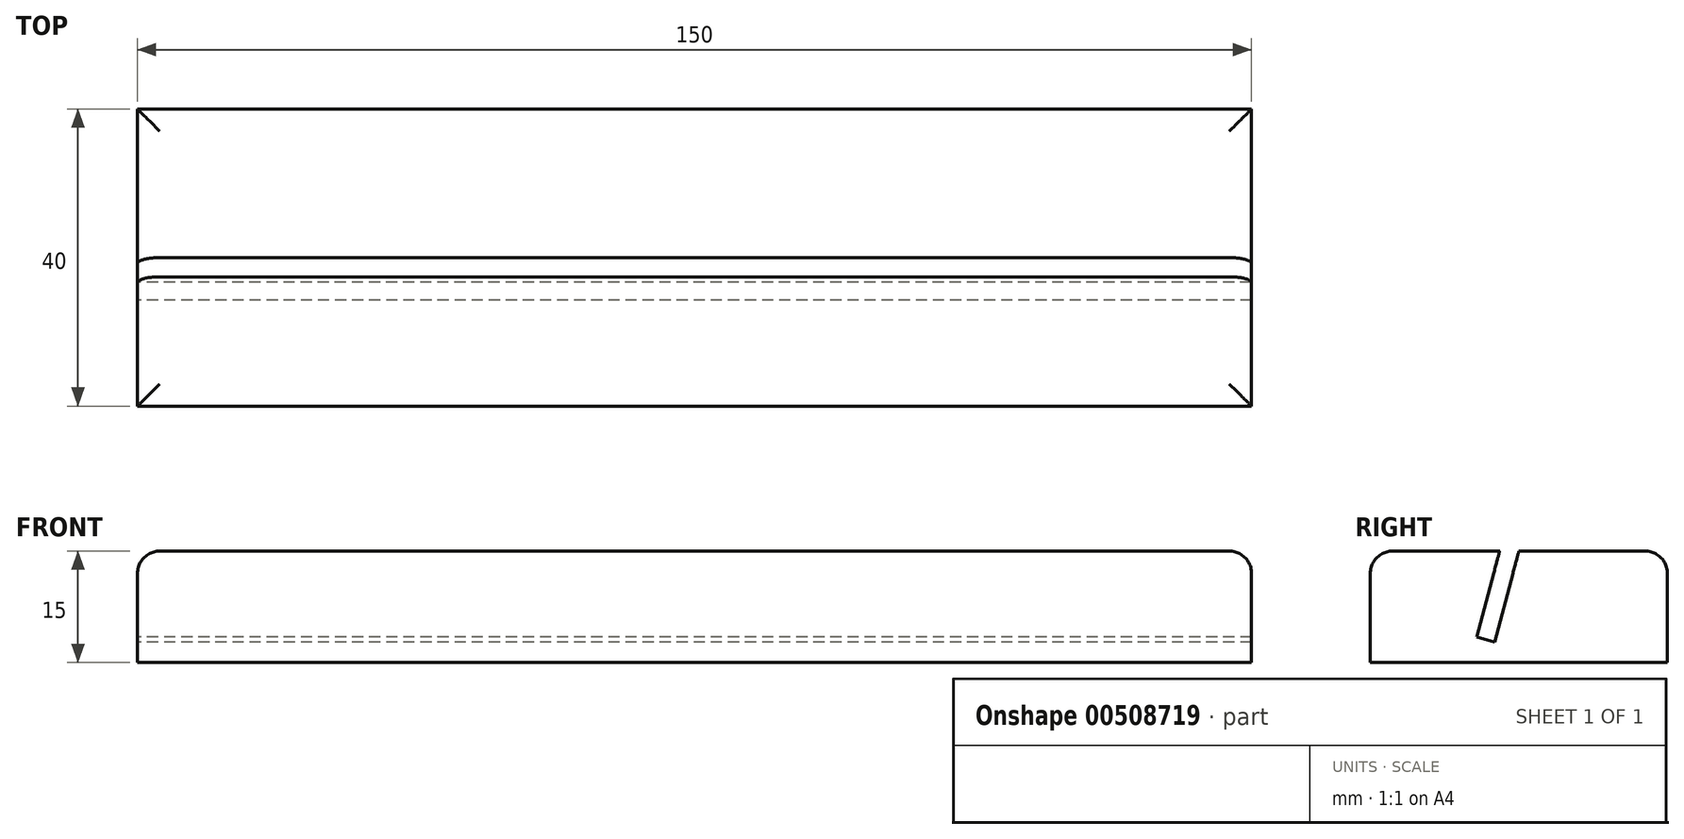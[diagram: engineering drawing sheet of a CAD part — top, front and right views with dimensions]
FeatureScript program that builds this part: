
annotation { "Feature Type Name" : "Feature", "Feature Type Description" : "" }
export const myFeature = defineFeature(function(context is Context, id is Id, definition is map)
    precondition{}
    {
        {
            var Q0;
            Q0=qCreatedBy(makeId("Top.planeOp"),FACE);
            var sketch = newSketch(context, id + "F0", { "sketchPlane" : qUnion([Q0])});
            skLineSegment(sketch, "E0.bottom", {"start": v(-75, 0) * mm, "end": v(75, 0) * mm});
            skLineSegment(sketch, "E0.top", {"start": v(-75, -40) * mm, "end": v(75, -40) * mm});
            skLineSegment(sketch, "E0.left", {"start": v(-75, 0) * mm, "end": v(-75, -40) * mm});
            skLineSegment(sketch, "E0.right", {"start": v(75, 0) * mm, "end": v(75, -40) * mm});
            skSolve(sketch);
        }
        {
            var Q0;
            Q0=makeQuery(id+"F0.imprint","IMPRINT",FACE,{"disambiguationData":[TD([[makeQuery(id+"F0.imprint","IMPRINT",EDGE,{"derivedFrom":sQuery(id+"F0.wireOp",EDGE,"E0.bottom")}),-1.0]])]});
            extrude(context, id + "F1", {"entities" : qUnion([Q0]), "depth" : 15 * mm});
        }
        {
            var Q0;
            Q0=makeQuery(id+"F1.opExtrude","SWEPT_FACE",FACE,{"disambiguationData":[OSD([sQuery(id+"F0.wireOp",EDGE,"E0.left")])]});
            var sketch = newSketch(context, id + "F2", { "sketchPlane" : qUnion([Q0])});
            skLineSegment(sketch, "E1", {"start": v(20, 15) * mm, "end": v(23.28, 2.76) * mm});
            skLineSegment(sketch, "E2", {"start": v(23.28, 2.76) * mm, "end": v(25.7, 3.4) * mm});
            skLineSegment(sketch, "E3", {"start": v(25.7, 3.4) * mm, "end": v(22.59, 15) * mm});
            skSolve(sketch);
        }
        {
            var Q0;
            {var subQ0=sQuery(id+"F2.wireOp",EDGE,"E1");Q0=makeQuery(id+"F2.imprint","IMPRINT",FACE,{"disambiguationData":[TD([[makeQuery(id+"F2.imprint","IMPRINT",EDGE,{"derivedFrom":subQ0}),1.0]])]});}
            extrude(context, id + "F3", {"entities" : qUnion([Q0]), "operationType" : NewBodyOperationType.REMOVE, "oppositeDirection" : true, "depth" : 150 * mm});
        }
        {
            var Q0;
            Q0=makeQuery(id+"F1.opExtrude","CAP_EDGE",EDGE,{"disambiguationData":[OSD([sQuery(id+"F0.wireOp",EDGE,"E0.bottom")])],"isStart":false});
            var Q1;
            {var subQ0=sQuery(id+"F0.wireOp",EDGE,"E0.bottom");var subQ1=sQuery(id+"F0.wireOp",EDGE,"E0.left");Q1=makeQuery(id+"F3.boolean.opBoolean","SPLIT",EDGE,{"disambiguationData":[TD([makeQuery(id+"F1.opExtrude","SWEPT_FACE",FACE,{"disambiguationData":[OSD([subQ0])]})])],"derivedFrom":makeQuery(id+"F1.opExtrude","CAP_EDGE",EDGE,{"disambiguationData":[OSD([subQ1])],"isStart":false})});}
            var Q2;
            {var subQ0=sQuery(id+"F0.wireOp",EDGE,"E0.bottom");var subQ1=sQuery(id+"F0.wireOp",EDGE,"E0.right");Q2=makeQuery(id+"F3.boolean.opBoolean","SPLIT",EDGE,{"disambiguationData":[TD([makeQuery(id+"F1.opExtrude","SWEPT_FACE",FACE,{"disambiguationData":[OSD([subQ0])]})])],"derivedFrom":makeQuery(id+"F1.opExtrude","CAP_EDGE",EDGE,{"disambiguationData":[OSD([subQ1])],"isStart":false})});}
            var Q3;
            {var subQ0=sQuery(id+"F0.wireOp",EDGE,"E0.right");var subQ1=sQuery(id+"F0.wireOp",EDGE,"E0.top");Q3=makeQuery(id+"F3.boolean.opBoolean","SPLIT",EDGE,{"disambiguationData":[TD([makeQuery(id+"F1.opExtrude","SWEPT_FACE",FACE,{"disambiguationData":[OSD([subQ1])]})])],"derivedFrom":makeQuery(id+"F1.opExtrude","CAP_EDGE",EDGE,{"disambiguationData":[OSD([subQ0])],"isStart":false})});}
            var Q4;
            Q4=makeQuery(id+"F1.opExtrude","CAP_EDGE",EDGE,{"disambiguationData":[OSD([sQuery(id+"F0.wireOp",EDGE,"E0.top")])],"isStart":false});
            var Q5;
            {var subQ0=sQuery(id+"F0.wireOp",EDGE,"E0.left");var subQ1=sQuery(id+"F0.wireOp",EDGE,"E0.top");Q5=makeQuery(id+"F3.boolean.opBoolean","SPLIT",EDGE,{"disambiguationData":[TD([makeQuery(id+"F1.opExtrude","SWEPT_FACE",FACE,{"disambiguationData":[OSD([subQ1])]})])],"derivedFrom":makeQuery(id+"F1.opExtrude","CAP_EDGE",EDGE,{"disambiguationData":[OSD([subQ0])],"isStart":false})});}
            fillet(context, id + "F4", {"entities" : qUnion([Q0, Q1, Q2, Q3, Q4, Q5]), "radius" : 3 * mm, "tangentPropagation" : true, "allowEdgeOverflow" : false});
        }
    });
